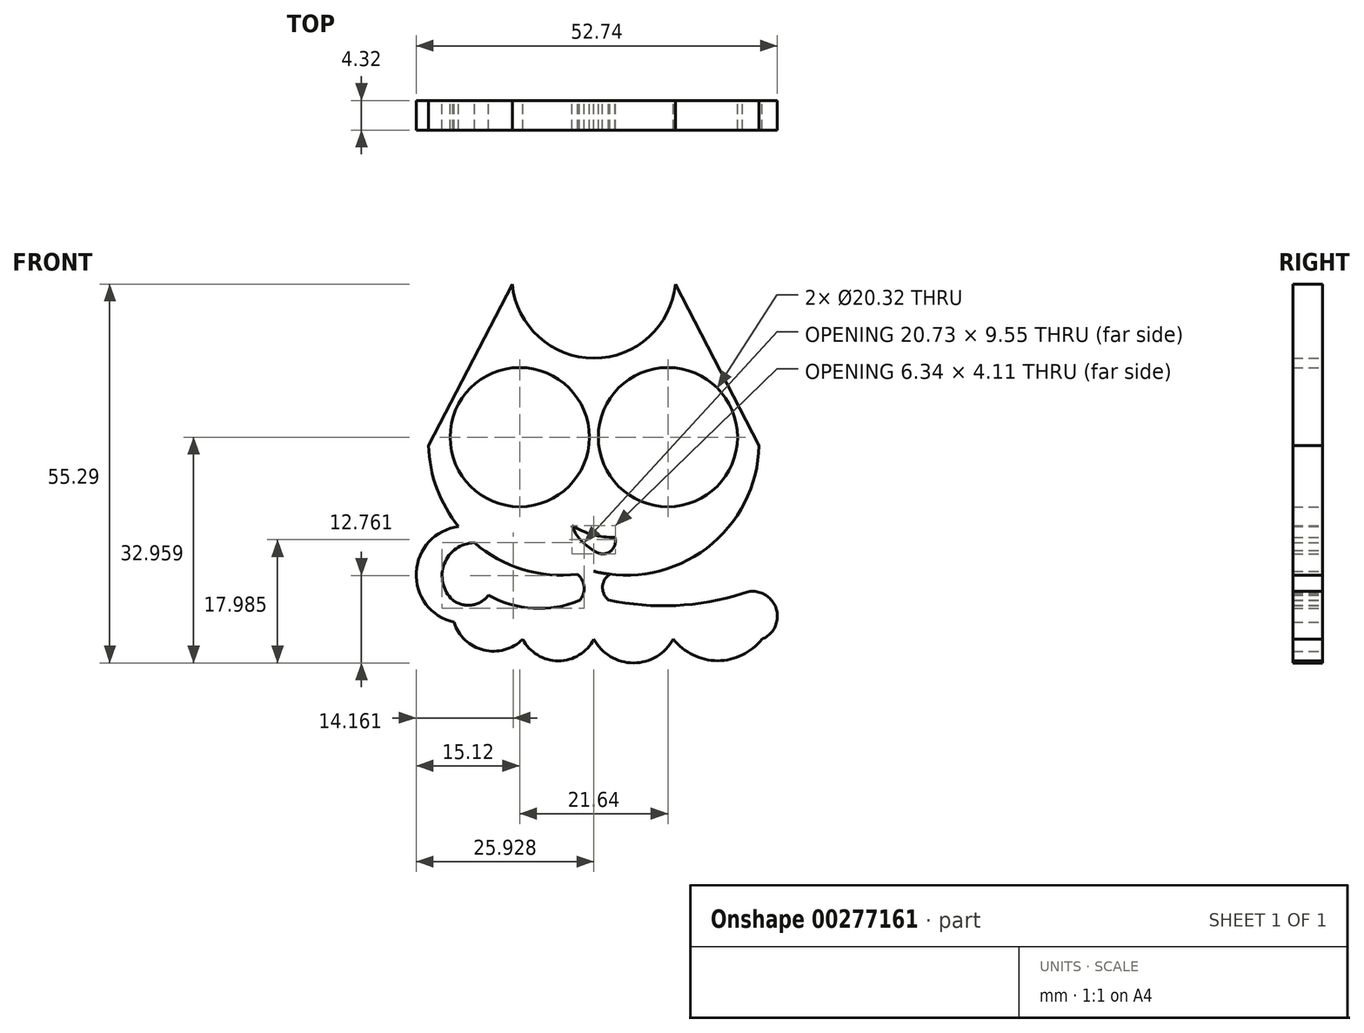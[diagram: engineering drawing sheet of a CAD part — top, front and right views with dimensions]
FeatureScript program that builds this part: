
annotation { "Feature Type Name" : "Feature", "Feature Type Description" : "" }
export const myFeature = defineFeature(function(context is Context, id is Id, definition is map)
    precondition{}
    {
        {
            var Q0;
            Q0=qCreatedBy(makeId("Front.planeOp"),FACE);
            var sketch = newSketch(context, id + "F0", { "sketchPlane" : qUnion([Q0])});
            skLineSegment(sketch, "E0", {"start": v(-11.92, 36.97) * mm, "end": v(-24.13, 13.43) * mm});
            skLineSegment(sketch, "E1", {"start": v(0, 56.08) * mm, "end": v(0, -39.2) * mm, "construction": true});
            skLineSegment(sketch, "E2.MirrorCS", {"start": v(11.92, 36.97) * mm, "end": v(24.13, 13.43) * mm});
            skArc(sketch, "E3", {"start": v(-11.92, 36.97) * mm, "mid": v(0, 26.17) * mm, "end": v(11.92, 36.97) * mm});
            skArc(sketch, "E4", {"start": v(-24.13, 13.43) * mm, "mid": v(-16.48, -1.55) * mm, "end": v(0, -4.94) * mm});
            skArc(sketch, "E5", {"start": v(0, -4.94) * mm, "mid": v(16.48, -1.55) * mm, "end": v(24.13, 13.43) * mm});
            skArc(sketch, "E6.MirrorCS", {"start": v(24.13, 13.43) * mm, "mid": v(16.48, -1.55) * mm, "end": v(0, -4.94) * mm});
            skArc(sketch, "E7", {"start": v(2.36, -5.37) * mm, "mid": v(1.27, -7.2) * mm, "end": v(2.14, -9.13) * mm});
            skArc(sketch, "E8", {"start": v(-2.1, -9.23) * mm, "mid": v(-1.41, -7.24) * mm, "end": v(-2.39, -5.38) * mm});
            skArc(sketch, "E9", {"start": v(2.14, -9.13) * mm, "mid": v(11.97, -9.94) * mm, "end": v(21.68, -8.2) * mm});
            skArc(sketch, "E10", {"start": v(24.56, -14.84) * mm, "mid": v(26.5, -10.06) * mm, "end": v(21.68, -8.2) * mm});
            skArc(sketch, "E11", {"start": v(11.6, -14.84) * mm, "mid": v(18.08, -18) * mm, "end": v(24.56, -14.84) * mm});
            skArc(sketch, "E12", {"start": v(0, -14.84) * mm, "mid": v(5.8, -18.32) * mm, "end": v(11.6, -14.84) * mm});
            skArc(sketch, "E13", {"start": v(-10.37, -14.84) * mm, "mid": v(-5.18, -18.02) * mm, "end": v(0, -14.84) * mm});
            skArc(sketch, "E14", {"start": v(-20.42, -12.38) * mm, "mid": v(-16.09, -16.44) * mm, "end": v(-10.37, -14.84) * mm});
            skArc(sketch, "E15", {"start": v(-19.74, 1.6) * mm, "mid": v(-25.93, -5.1) * mm, "end": v(-20.42, -12.38) * mm});
            skArc(sketch, "E16", {"start": v(-15.4, -8.44) * mm, "mid": v(-8.83, -10.33) * mm, "end": v(-2.1, -9.23) * mm});
            skArc(sketch, "E17", {"start": v(-17.42, -0.78) * mm, "mid": v(-21.84, -3.87) * mm, "end": v(-20.62, -9.13) * mm});
            skArc(sketch, "E18", {"start": v(-20.62, -9.13) * mm, "mid": v(-17.86, -9.88) * mm, "end": v(-15.4, -8.44) * mm});
            skCircle(sketch, "E19", {"center": v(-10.82, 14.64) * mm, "radius": 10.16 * mm});
            skPoint(sketch, "E19.first.point", {"position": v(-1.29, 11.13) * mm});
            skPoint(sketch, "E19.second.point", {"position": v(-19.4, 20.08) * mm});
            skPoint(sketch, "E19.third.point", {"position": v(-9.5, 24.71) * mm});
            skCircle(sketch, "E20.MirrorC", {"center": v(10.82, 14.64) * mm, "radius": 10.16 * mm});
            skArc(sketch, "E21", {"start": v(0, -1.9) * mm, "mid": v(2.26, -2.12) * mm, "end": v(3.1, 0) * mm});
            skArc(sketch, "E22", {"start": v(-3.18, 1.72) * mm, "mid": v(-1.93, -0.39) * mm, "end": v(0, -1.9) * mm});
            skArc(sketch, "E23", {"start": v(-3.18, 1.72) * mm, "mid": v(-0.17, 0.42) * mm, "end": v(3.1, 0) * mm});
            skSolve(sketch);
        }
        {
            var Q0;
            {var subQ9=sQuery(id+"F0.wireOp",EDGE,"E0");Q0=makeQuery(id+"F0.imprint","IMPRINT",FACE,{"disambiguationData":[TD([[makeQuery(id+"F0.imprint","IMPRINT",EDGE,{"derivedFrom":subQ9}),1.0]])]});}
            var Q1;
            {var subQ1=sQuery(id+"F0.wireOp",EDGE,"E8");Q1=makeQuery(id+"F0.imprint","IMPRINT",FACE,{"disambiguationData":[TD([[makeQuery(id+"F0.imprint","IMPRINT",EDGE,{"derivedFrom":subQ1}),-1.0]])]});}
            extrude(context, id + "F1", {"entities" : qUnion([Q0, Q1]), "depth" : 4.32 * mm});
        }
    });
